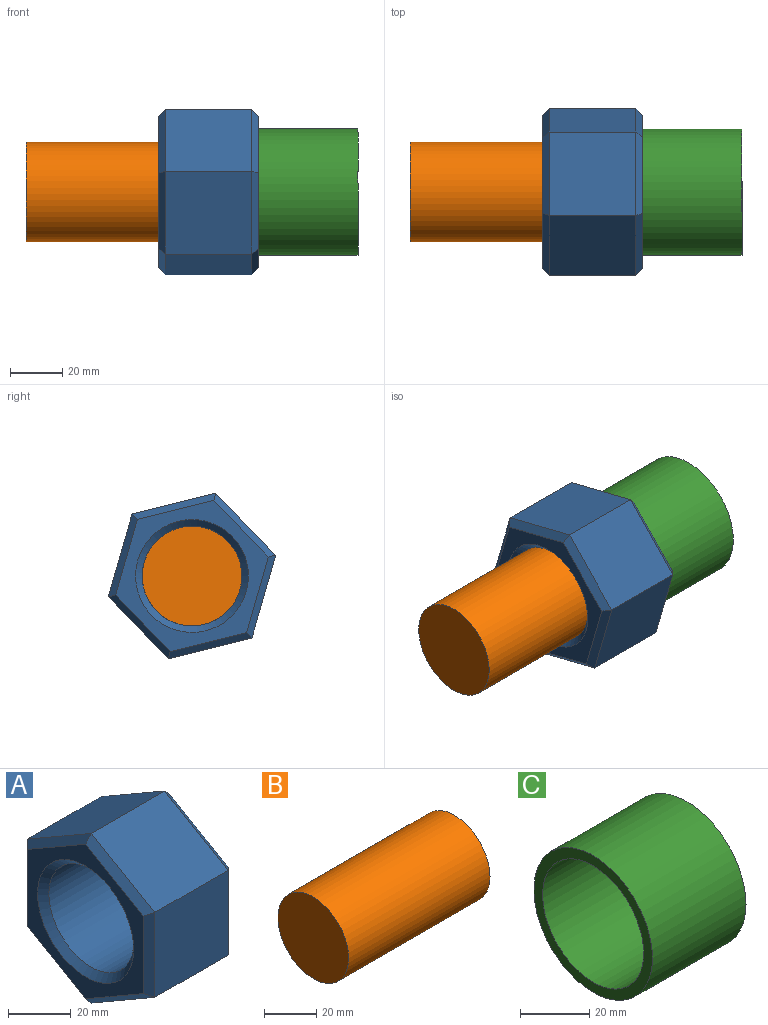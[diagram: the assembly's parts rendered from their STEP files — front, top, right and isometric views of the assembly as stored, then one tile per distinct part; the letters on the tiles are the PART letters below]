
ASSEMBLY  parts=3 mates=2
PART A: 23 faces, bbox 38.1x57.2x66 mm
  f0: plane 33.02x28.58mm, normal (0,-0.5,0.87), area 1089.5mm2, adj f1,f5,f14,f21
  f1: plane 33.02x28.58mm, normal (0,0.5,0.87), area 1089.5mm2, adj f0,f2,f12,f19
  f2: plane 33.02x33mm, normal (0,1,0), area 1089.5mm2, adj f1,f3,f10,f17
  f3: plane 33.02x28.58mm, normal (0,0.5,-0.87), area 1089.5mm2, adj f2,f4,f9,f16
  f4: plane 33.02x28.58mm, normal (0,-0.5,-0.87), area 1089.5mm2, adj f3,f5,f11,f18
  f5: plane 33.02x33mm, normal (0,-1,0), area 1089.5mm2, adj f0,f4,f13,f20
  f6: cylinder r=19.05mm len=38.1mm, axis (1,0,0), area 3952.3mm2, adj f15,f22
  f7: plane 60.13x52.07mm, normal (-1,0,0), area 883.7mm2, adj f16,f17,f18,f19,f20,f21,f22
  f8: plane 60.13x52.07mm, normal (1,0,0), area 883.7mm2, adj f9,f10,f11,f12,f13,f14,f15
  f9: plane 28.58x17.96mm, normal (0.71,0.35,-0.61), area 113.3mm2, adj f3,f8,f10,f11
  f10: plane 33x2.54mm, normal (0.71,0.71,0), area 113.3mm2, adj f2,f8,f9,f12
  f11: plane 28.58x17.96mm, normal (0.71,-0.35,-0.61), area 113.3mm2, adj f4,f8,f9,f13
  f12: plane 28.58x17.96mm, normal (0.71,0.35,0.61), area 113.3mm2, adj f1,f8,f10,f14
  f13: plane 33x2.54mm, normal (0.71,-0.71,0), area 113.3mm2, adj f5,f8,f11,f14
  f14: plane 28.58x17.96mm, normal (0.71,-0.35,0.61), area 113.3mm2, adj f0,f8,f12,f13
  f15: cone r=21.59mm half-angle=45deg, axis (1,0,0), area 458.6mm2, adj f6,f8
  f16: plane 28.58x17.96mm, normal (-0.71,0.35,-0.61), area 113.3mm2, adj f3,f7,f17,f18
  f17: plane 33x2.54mm, normal (-0.71,0.71,0), area 113.3mm2, adj f2,f7,f16,f19
  f18: plane 28.58x17.96mm, normal (-0.71,-0.35,-0.61), area 113.3mm2, adj f4,f7,f16,f20
  f19: plane 28.58x17.96mm, normal (-0.71,0.35,0.61), area 113.3mm2, adj f1,f7,f17,f21
  f20: plane 33x2.54mm, normal (-0.71,-0.71,0), area 113.3mm2, adj f5,f7,f18,f21
  f21: plane 28.58x17.96mm, normal (-0.71,-0.35,0.61), area 113.3mm2, adj f0,f7,f19,f20
  f22: cone r=19.05mm half-angle=45deg, axis (-1,0,0), area 458.6mm2, adj f6,f7
PART B: 3 faces, bbox 76.2x38.1x38.1 mm
  f0: cylinder r=19.05mm len=76.2mm, axis (1,0,0), area 9120.7mm2, adj f1,f2
  f1: plane 38.1x38.1mm, normal (-1,0,0), area 1140.1mm2, adj f0
  f2: plane 38.1x38.1mm, normal (1,0,0), area 1140.1mm2, adj f0
PART C: 4 faces, bbox 38.1x48.3x48.3 mm
  f0: cylinder r=20.57mm len=41.15mm, axis (-1,0,0), area 4925.2mm2, adj f2,f3
  f1: cylinder r=24.13mm len=48.26mm, axis (-1,0,0), area 5776.5mm2, adj f2,f3
  f2: plane 48.26x48.26mm, normal (1,0,0), area 499.4mm2, adj f0,f1
  f3: plane 48.26x48.26mm, normal (-1,0,0), area 499.4mm2, adj f0,f1
PLACE A rot(axis=(-1,0,0),44deg) t=(435.61,-8.26,1.13)mm
PLACE B rot(axis=(1,0,0),136deg) t=(346.71,-8.26,1.13)mm
PLACE C rot(axis=(-1,0,0),134deg) t=(435.61,-8.26,1.13)mm
MATE cylindrical A.f6 <-> B.f0  axis (1,0,0) through (231.9,-8.26,1.13)mm
MATE fastened A.f6 <-> C.f0  axis (1,0,0) through (250.95,-8.26,1.13)mm
